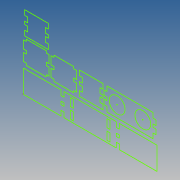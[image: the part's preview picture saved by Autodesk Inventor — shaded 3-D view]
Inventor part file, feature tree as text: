
AUTODESK INVENTOR PART (.ipt)
format: ipt  version: 2020 (Build 240168000, 168)  size: 114,176 bytes
history: native  units: mm
features: sketch x1
ambient origin geometry x8: Origin, YZ Plane, XZ Plane, XY Plane, X Axis, Y Axis, Z Axis, Center Point
feature tree (1):
  sketch  "Sketch1"
